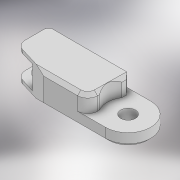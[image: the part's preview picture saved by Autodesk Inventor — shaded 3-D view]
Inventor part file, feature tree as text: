
AUTODESK INVENTOR PART (.ipt)
format: ipt  version: 2022 (Build 260153000, 153)  size: 239,616 bytes
history: native  units: mm
features: sketch x7, extrude x7, projected_geometry x5, fillet x3, chamfer x3, plane x1
ambient origin geometry x8: Origin, YZ Plane, XZ Plane, XY Plane, X Axis, Y Axis, Z Axis, Center Point
bodies: Solid1 (feature_tree)
feature tree (26):
  sketch  "Sketch2"  dims[d0=4.4mm d1=13.5mm]
  extrude  "Extrusion1"  Depth=13.5mm
  extrude  "Extrusion2"  Depth=8.85mm TaperAngle=0.0deg
  extrude  "Extrusion3"  Depth=1.0mm
  extrude  "Extrusion4"  Depth=8.85mm TaperAngle=0.0deg
  extrude  "Extrusion5"  Depth=8.0mm TaperAngle=0.0deg
  extrude  "Extrusion6"  Depth=8.0mm TaperAngle=0.0deg
  extrude  "Extrusion7"  Depth=1.0mm TaperAngle=0.0deg
  sketch  "Sketch8"  dims[d17=10.25mm d18=0.0mm d19=10.25mm d20=0.0mm d21=3.0mm d22=2.0mm d23=2.0mm d24=45.0deg d25=2.0mm d26=2.0mm d27=45.0deg d28=3.0mm d29=1.0mm d30=2.0mm d31=45.0deg d32=1.0mm]
  fillet  "Fillet1"  Radius=3.0mm
  chamfer  "Chamfer1"  Distance=2.0mm Angle=45.0deg
  chamfer  "Chamfer2"  Distance=2.0mm Angle=45.0deg
  fillet  "Fillet2"  Radius=3.0mm
  chamfer  "Chamfer3"  Distance=1.0mm Angle=45.0deg
  fillet  "Fillet3"  Radius=1.0mm
  plane  "Work Plane1"
  sketch  "Sketch3"  dims[d2=3.85mm d3=0.0mm d4=8.85mm d5=0.0mm]
  projected_geometry  "Projected Loop1"
  sketch  "Sketch4"  dims[d6=0.5mm d7=1.0mm]
  projected_geometry  "Projected Loop2"
  sketch  "Sketch5"  dims[d8=12.5mm d9=8.85mm d10=0.0mm]
  projected_geometry  "Projected Loop3"
  sketch  "Sketch6"  dims[d11=1.0mm d12=8.0mm d13=0.0mm]
  sketch  "Sketch7"  dims[d14=5.1mm d15=8.0mm d16=0.0mm]
  projected_geometry  "Projected Loop5"
  projected_geometry  "Projected Loop6"
